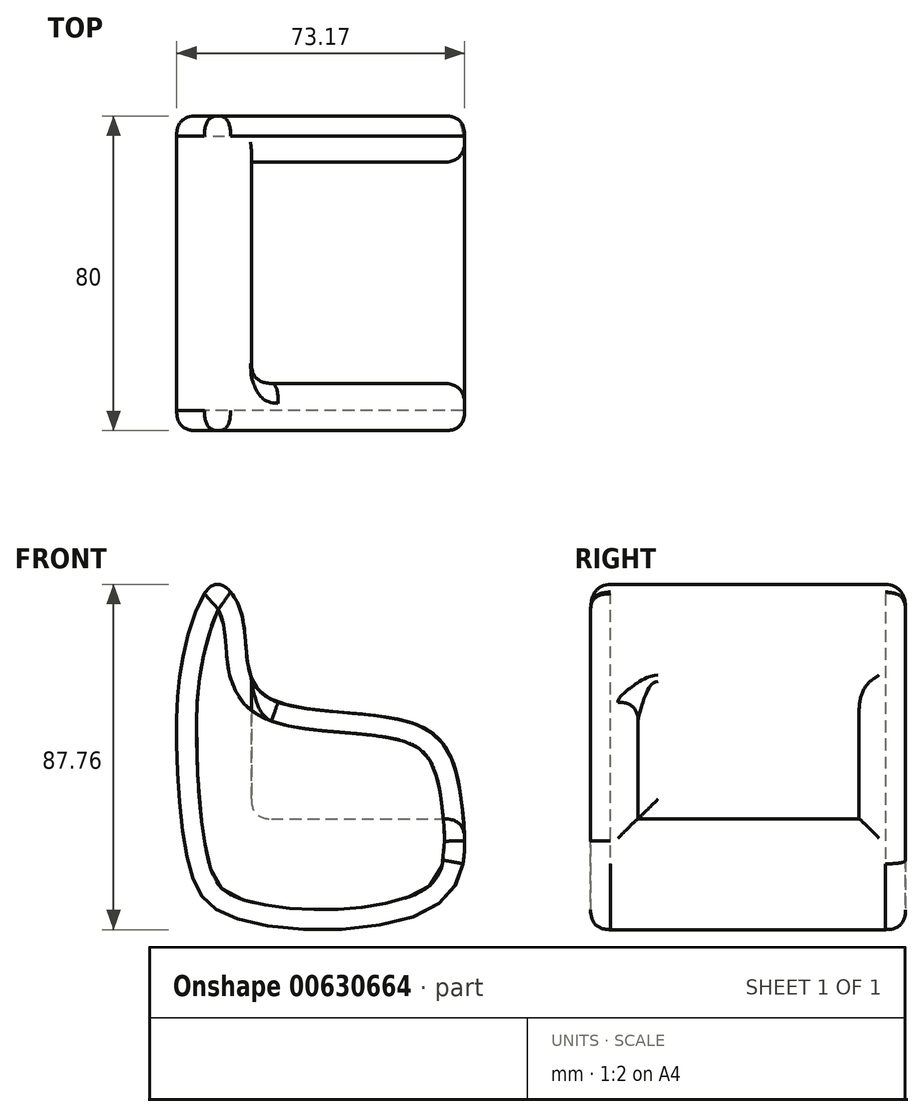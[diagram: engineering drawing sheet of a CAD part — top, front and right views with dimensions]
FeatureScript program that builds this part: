
annotation { "Feature Type Name" : "Feature", "Feature Type Description" : "" }
export const myFeature = defineFeature(function(context is Context, id is Id, definition is map)
    precondition{}
    {
        {
            var Q0;
            Q0=qCreatedBy(makeId("Front.planeOp"),FACE);
            var sketch = newSketch(context, id + "F0", { "sketchPlane" : qUnion([Q0])});
            skFitSpline(sketch, "E0", {"points": [v(-24.57, -48.67) * mm, v(-36.46, -35.2) * mm, v(-39.6, 0) * mm, v(-37.4, 20.5) * mm, v(-29.89, 36.15) * mm, v(-23, 28.32) * mm, v(-17.68, 8.3) * mm, v(22.7, 0) * mm, v(33.02, -21.13) * mm, v(27.07, -44.91) * mm, v(-24.57, -48.67) * mm]});
            skSolve(sketch);
        }
        {
            var Q0;
            Q0 = qSketchRegion(id + "F0", true);
            extrude(context, id + "F1", {"entities" : qUnion([Q0]), "depth" : 80 * mm, "offsetDistance" : 25.4 * mm});
        }
        {
            var Q0;
            Q0=qCreatedBy(makeId("Top.planeOp"),FACE);
            cPlane(context, id + "F2", {"entities" : qUnion([Q0]), "cplaneType" : CPlaneType.OFFSET, "offset" : 50 * mm, "width" : 152.4 * mm, "height" : 152.4 * mm});
        }
        {
            var Q0;
            Q0=qCreatedBy(id+"F2.planeOp",FACE);
            var sketch = newSketch(context, id + "F3", { "sketchPlane" : qUnion([Q0])});
            skLineSegment(sketch, "E1.bottom", {"start": v(-20.6, -11.78) * mm, "end": v(38, -11.78) * mm});
            skLineSegment(sketch, "E1.top", {"start": v(-20.6, -67.95) * mm, "end": v(38, -67.95) * mm});
            skLineSegment(sketch, "E1.left", {"start": v(-20.6, -11.78) * mm, "end": v(-20.6, -67.95) * mm});
            skLineSegment(sketch, "E1.right", {"start": v(38, -11.78) * mm, "end": v(38, -67.95) * mm});
            skSolve(sketch);
        }
        {
            var Q0;
            Q0 = qSketchRegion(id + "F3", true);
            extrude(context, id + "F4", {"entities" : qUnion([Q0]), "operationType" : NewBodyOperationType.REMOVE, "oppositeDirection" : true, "depth" : 73.4 * mm, "offsetDistance" : 25.4 * mm});
        }
        {
            var Q0;
            Q0=makeQuery(id+"F1.opExtrude","SWEPT_FACE",FACE,{"disambiguationData":[OSD([sQuery(id+"F0.wireOp",EDGE,"E0")])]});
            var Q1;
            Q1=makeQuery(id+"F4.boolean.opBoolean","INTERSECT",EDGE,{"derivedFrom":[makeQuery(id+"F1.opExtrude","SWEPT_FACE",FACE,{"disambiguationData":[OSD([sQuery(id+"F0.wireOp",EDGE,"E0")])]}),makeQuery(id+"F4.opExtrude","SWEPT_FACE",FACE,{"disambiguationData":[OSD([sQuery(id+"F3.wireOp",EDGE,"E1.top")])]})]});
            var Q2;
            Q2=makeQuery(id+"F4.boolean.opBoolean","COPY",EDGE,{"derivedFrom":makeQuery(id+"F4.opExtrude","SWEPT_EDGE",EDGE,{"disambiguationData":[OSD([sQuery(id+"F3.wireOp",EDGE,"E1.top"),sQuery(id+"F3.wireOp",EDGE,"E1.left")])]})});
            var Q3;
            Q3=makeQuery(id+"F4.boolean.opBoolean","INTERSECT",EDGE,{"derivedFrom":[makeQuery(id+"F1.opExtrude","SWEPT_FACE",FACE,{"disambiguationData":[OSD([sQuery(id+"F0.wireOp",EDGE,"E0")])]}),makeQuery(id+"F4.opExtrude","SWEPT_FACE",FACE,{"disambiguationData":[OSD([sQuery(id+"F3.wireOp",EDGE,"E1.left")])]})]});
            var Q4;
            Q4=makeQuery(id+"F4.boolean.opBoolean","COPY",EDGE,{"derivedFrom":makeQuery(id+"F4.opExtrude","CAP_EDGE",EDGE,{"disambiguationData":[OSD([sQuery(id+"F3.wireOp",EDGE,"E1.left")])],"isStart":false})});
            var Q5;
            Q5=makeQuery(id+"F4.boolean.opBoolean","INTERSECT",EDGE,{"derivedFrom":[makeQuery(id+"F1.opExtrude","SWEPT_FACE",FACE,{"disambiguationData":[OSD([sQuery(id+"F0.wireOp",EDGE,"E0")])]}),makeQuery(id+"F4.opExtrude","SWEPT_FACE",FACE,{"disambiguationData":[OSD([sQuery(id+"F3.wireOp",EDGE,"E1.bottom")])]})]});
            fillet(context, id + "F5", {"entities" : qUnion([Q0, Q1, Q2, Q3, Q4, Q5]), "radius" : 5.08 * mm, "tangentPropagation" : true, "rho" : 0.5, "crossSection" : FilletCrossSection.CONIC, "allowEdgeOverflow" : false});
        }
    });
